# Revit family: Sanitary_Taps-Mixers_AXOR_48430XXX-AXOR-One-3-hole-bath-mixer-for-concealed-installation-wall-mounted-with-cross-handles_NEW
name_source: partatom
category: Plumbing Fixtures
units: mm (PartAtom-declared; Revit-internal decimal feet)

## family parameters
Cut with Voids When Loaded = Yes
Host = Face
Maintain Annotation Orientation = No
OmniClass Number = 23.31.11.00
OmniClass Title = Faucets
Part Type = Normal
Room Calculation Point = No
Round Connector Dimension = Use Diameter
Shared = No

## types (1)
- 48430XXX AXOR One 3-hole bath mixer for concealed installation wall-mounted with cross handles
    Default Elevation = 1219 mm
    Description = AXOR One 3-hole bath mixer for concealed installation wall-mounted with cross handles
    Manufacturer = AXOR
    Material 1 = AXOR - Metal - 000 Chrome
    Model = 48430XXX
    Product Page URL = https://www.axor-design.com
    Product data url = https://bimobject.com
    URL = https://www.axor-design.com
    Version = 1

## geometry (parser evidence)
native form markers: Sweep x2
no freeform markers — native parametric forms only
